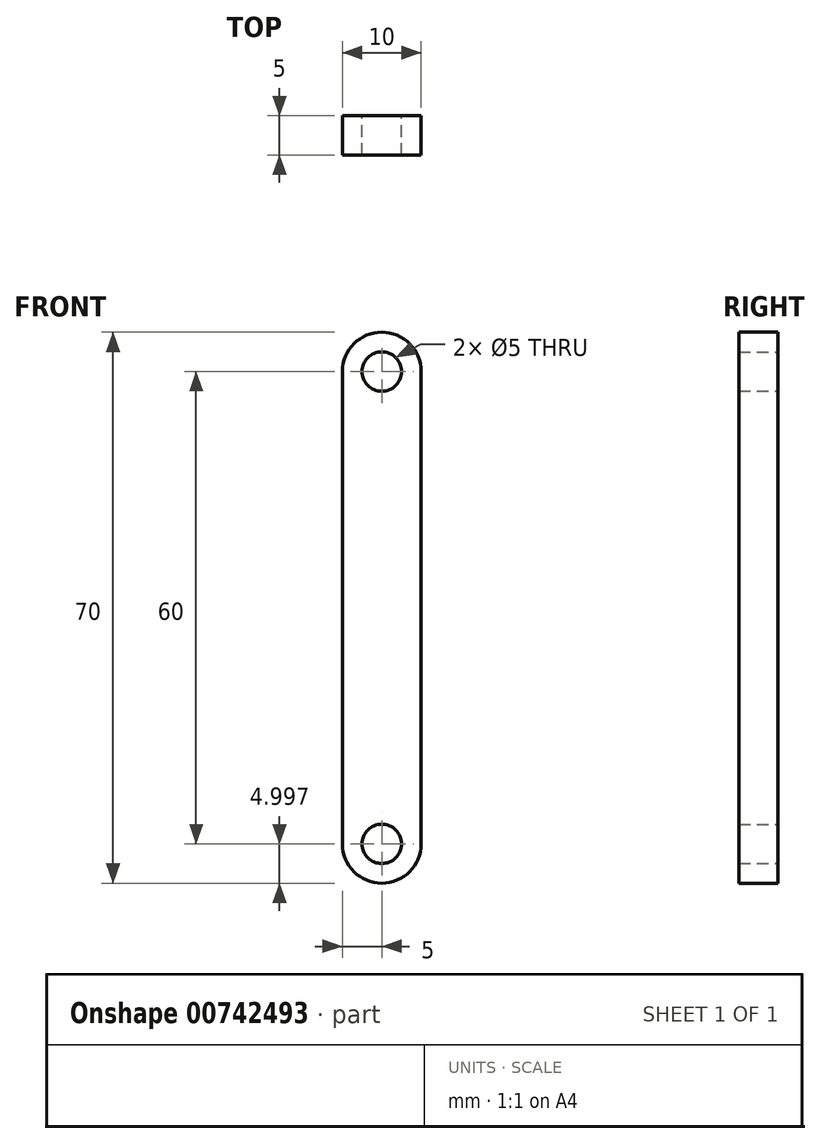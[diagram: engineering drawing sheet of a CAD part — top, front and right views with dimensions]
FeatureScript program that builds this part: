
annotation { "Feature Type Name" : "Feature", "Feature Type Description" : "" }
export const myFeature = defineFeature(function(context is Context, id is Id, definition is map)
    precondition{}
    {
        {
            var Q0;
            Q0=qCreatedBy(makeId("Front.planeOp"),FACE);
            var sketch = newSketch(context, id + "F0", { "sketchPlane" : qUnion([Q0])});
            skLineSegment(sketch, "E0", {"start": v(0, 50.6) * mm, "end": v(0, -30.27) * mm, "construction": true});
            skCircle(sketch, "E1", {"center": v(0, -19.48) * mm, "radius": 5 * mm});
            skCircle(sketch, "E2", {"center": v(0, 40.52) * mm, "radius": 5 * mm});
            skLineSegment(sketch, "E3", {"start": v(-5, 40.52) * mm, "end": v(-5, -19.48) * mm});
            skLineSegment(sketch, "E4", {"start": v(5, 40.52) * mm, "end": v(5, -19.48) * mm});
            skCircle(sketch, "E5", {"center": v(0, 40.52) * mm, "radius": 2.5 * mm});
            skCircle(sketch, "E6", {"center": v(0, -19.48) * mm, "radius": 2.5 * mm});
            skSolve(sketch);
        }
        {
            var Q0;
            {var subQ0=sQuery(id+"F0.wireOp",EDGE,"E3");Q0=makeQuery(id+"F0.imprint","IMPRINT",FACE,{"disambiguationData":[TD([[makeQuery(id+"F0.imprint","IMPRINT",EDGE,{"derivedFrom":subQ0}),1.0]])]});}
            var Q1;
            Q1=makeQuery(id+"F0.imprint","IMPRINT",FACE,{"disambiguationData":[TD([[makeQuery(id+"F0.imprint","IMPRINT",EDGE,{"derivedFrom":sQuery(id+"F0.wireOp",EDGE,"E5")}),-1.0]])]});
            var Q2;
            Q2=makeQuery(id+"F0.imprint","IMPRINT",FACE,{"disambiguationData":[TD([[makeQuery(id+"F0.imprint","IMPRINT",EDGE,{"derivedFrom":sQuery(id+"F0.wireOp",EDGE,"E6")}),-1.0]])]});
            extrude(context, id + "F1", {"entities" : qUnion([Q0, Q1, Q2]), "depth" : 5 * mm, "offsetDistance" : 25 * mm});
        }
    });
